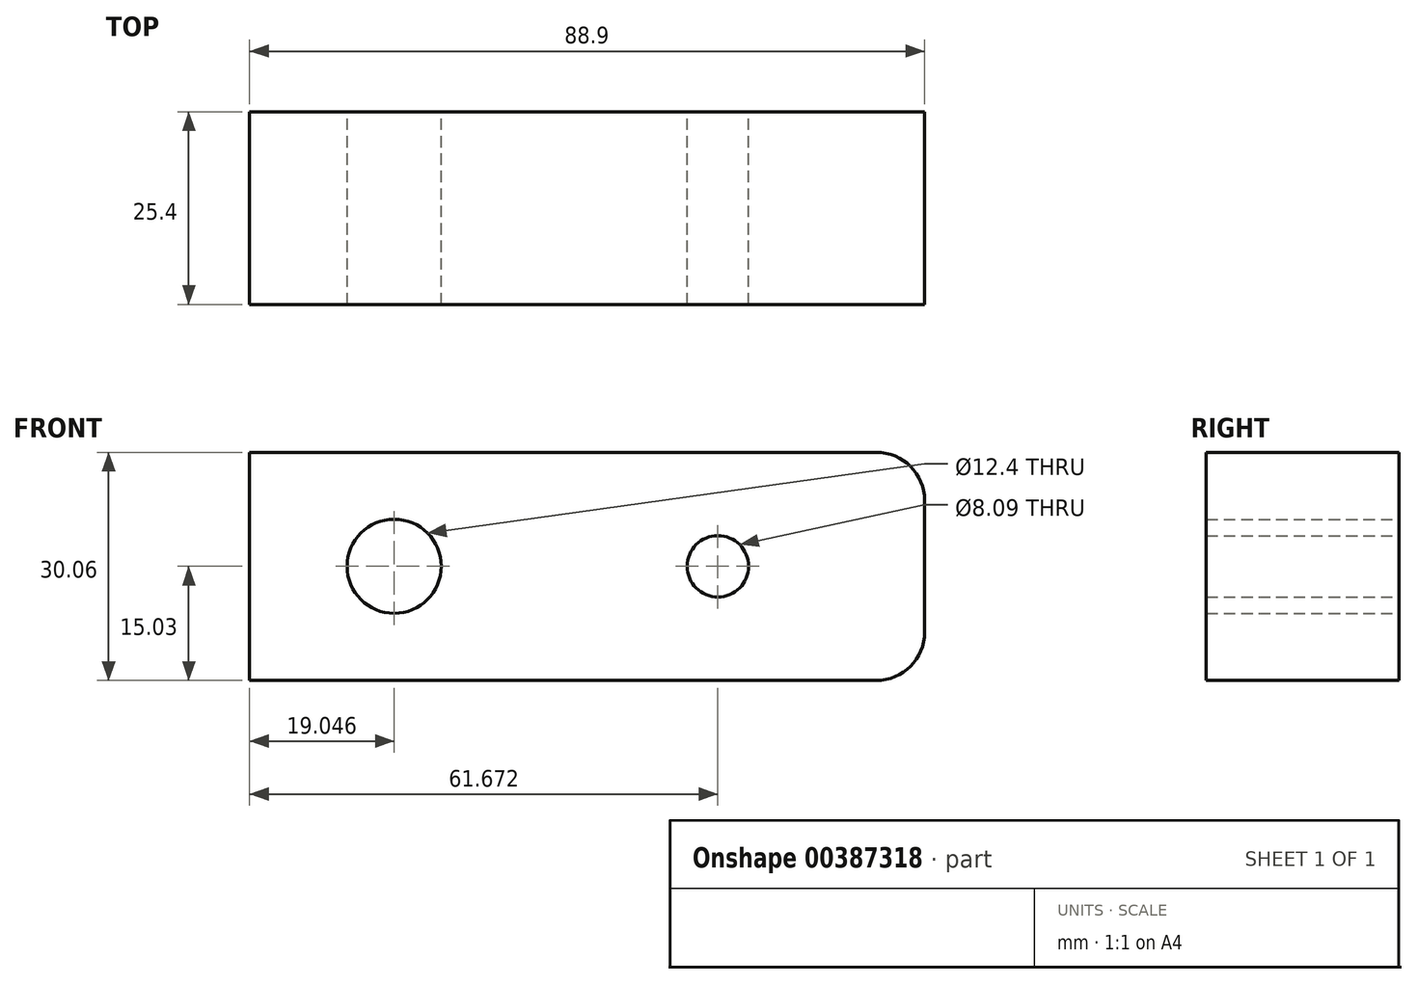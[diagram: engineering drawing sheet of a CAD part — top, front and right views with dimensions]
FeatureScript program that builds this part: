
annotation { "Feature Type Name" : "Feature", "Feature Type Description" : "" }
export const myFeature = defineFeature(function(context is Context, id is Id, definition is map)
    precondition{}
    {
        {
            var Q0;
            Q0=qCreatedBy(makeId("Front.planeOp"),FACE);
            var sketch = newSketch(context, id + "F0", { "sketchPlane" : qUnion([Q0])});
            skLineSegment(sketch, "E0.bottom", {"start": v(-46.78, 15.03) * mm, "end": v(35.77, 15.03) * mm});
            skLineSegment(sketch, "E0.top", {"start": v(-46.78, -15.03) * mm, "end": v(35.77, -15.03) * mm});
            skLineSegment(sketch, "E0.left", {"start": v(-46.78, 15.03) * mm, "end": v(-46.78, -15.03) * mm});
            skLineSegment(sketch, "E0.right", {"start": v(42.12, 8.68) * mm, "end": v(42.12, -8.68) * mm});
            skPoint(sketch, "E0.middle", {"position": v(-2.33, 0) * mm});
            skCircle(sketch, "E1", {"center": v(-27.73, 0) * mm, "radius": 6.2 * mm});
            skCircle(sketch, "E2", {"center": v(14.9, 0) * mm, "radius": 4.05 * mm});
            skPoint(sketch, "E3.visualSharp", {"position": v(42.12, 15.03) * mm});
            skArc(sketch, "E3.filletArc", {"start": v(42.12, 8.68) * mm, "mid": v(40.26, 13.17) * mm, "end": v(35.77, 15.03) * mm});
            skPoint(sketch, "E4.visualSharp", {"position": v(42.12, -15.03) * mm});
            skArc(sketch, "E4.filletArc", {"start": v(35.77, -15.03) * mm, "mid": v(40.26, -13.17) * mm, "end": v(42.12, -8.68) * mm});
            skSolve(sketch);
        }
        {
            var Q0;
            Q0 = qSketchRegion(id + "F0", true);
            extrude(context, id + "F1", {"entities" : qUnion([Q0]), "depth" : 25.4 * mm, "symmetric" : true});
        }
    });
